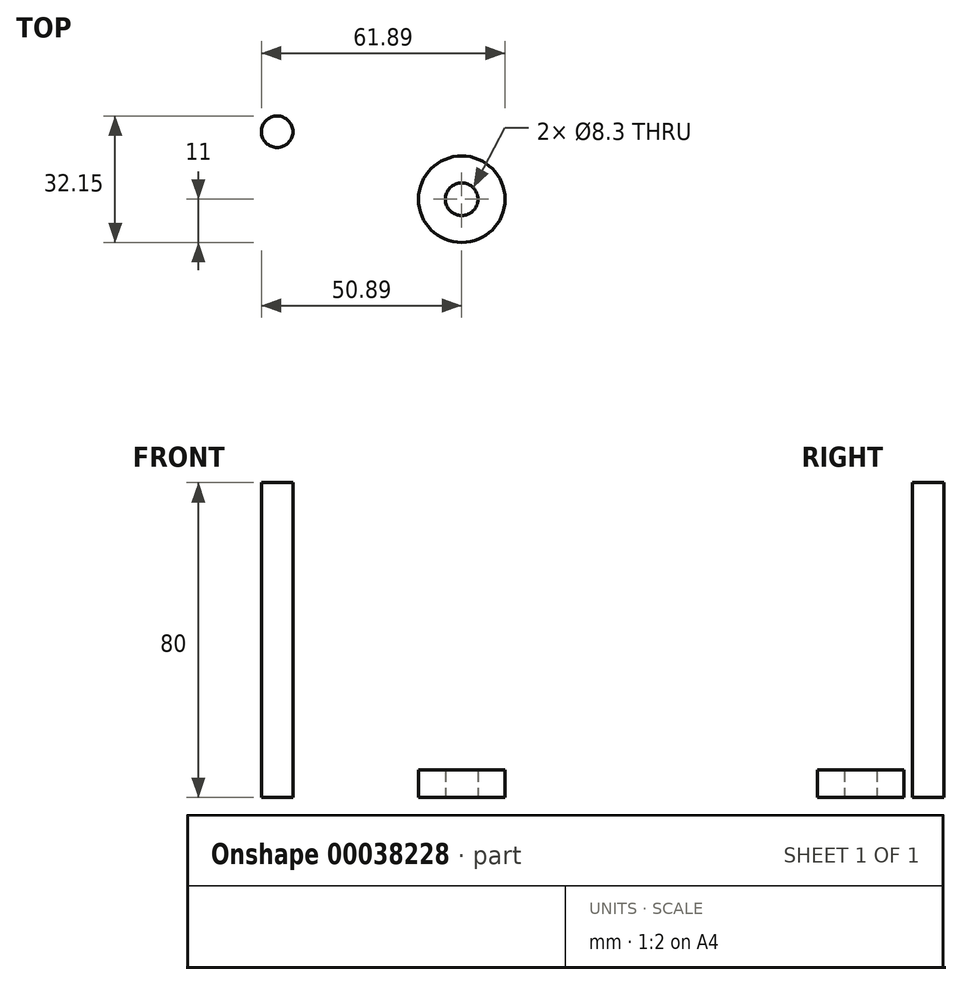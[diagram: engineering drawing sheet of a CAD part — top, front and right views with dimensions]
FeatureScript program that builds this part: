
annotation { "Feature Type Name" : "Feature", "Feature Type Description" : "" }
export const myFeature = defineFeature(function(context is Context, id is Id, definition is map)
    precondition{}
    {
        {
            var Q0;
            Q0=qCreatedBy(makeId("Top.planeOp"),FACE);
            var sketch = newSketch(context, id + "F0", { "sketchPlane" : qUnion([Q0])});
            skCircle(sketch, "E0", {"center": v(0, 0) * mm, "radius": 11 * mm});
            skCircle(sketch, "E1", {"center": v(0, 0) * mm, "radius": 4.15 * mm});
            skSolve(sketch);
        }
        {
            var Q0;
            Q0=makeQuery(id+"F0.imprint","IMPRINT",FACE,{"disambiguationData":[TD([[makeQuery(id+"F0.imprint","IMPRINT",EDGE,{"derivedFrom":sQuery(id+"F0.wireOp",EDGE,"E0")}),1.0]])]});
            extrude(context, id + "F1", {"entities" : qUnion([Q0]), "depth" : 7 * mm});
        }
        {
            var Q0;
            Q0=qCreatedBy(makeId("Top.planeOp"),FACE);
            var sketch = newSketch(context, id + "F2", { "sketchPlane" : qUnion([Q0])});
            skCircle(sketch, "E2", {"center": v(-46.9, 17.15) * mm, "radius": 4 * mm});
            skSolve(sketch);
        }
        {
            var Q0;
            Q0=makeQuery(id+"F2.imprint","IMPRINT",FACE,{"disambiguationData":[TD([[makeQuery(id+"F2.imprint","IMPRINT",EDGE,{"derivedFrom":sQuery(id+"F2.wireOp",EDGE,"E2")}),1.0]])]});
            extrude(context, id + "F3", {"entities" : qUnion([Q0]), "depth" : 80 * mm});
        }
    });
